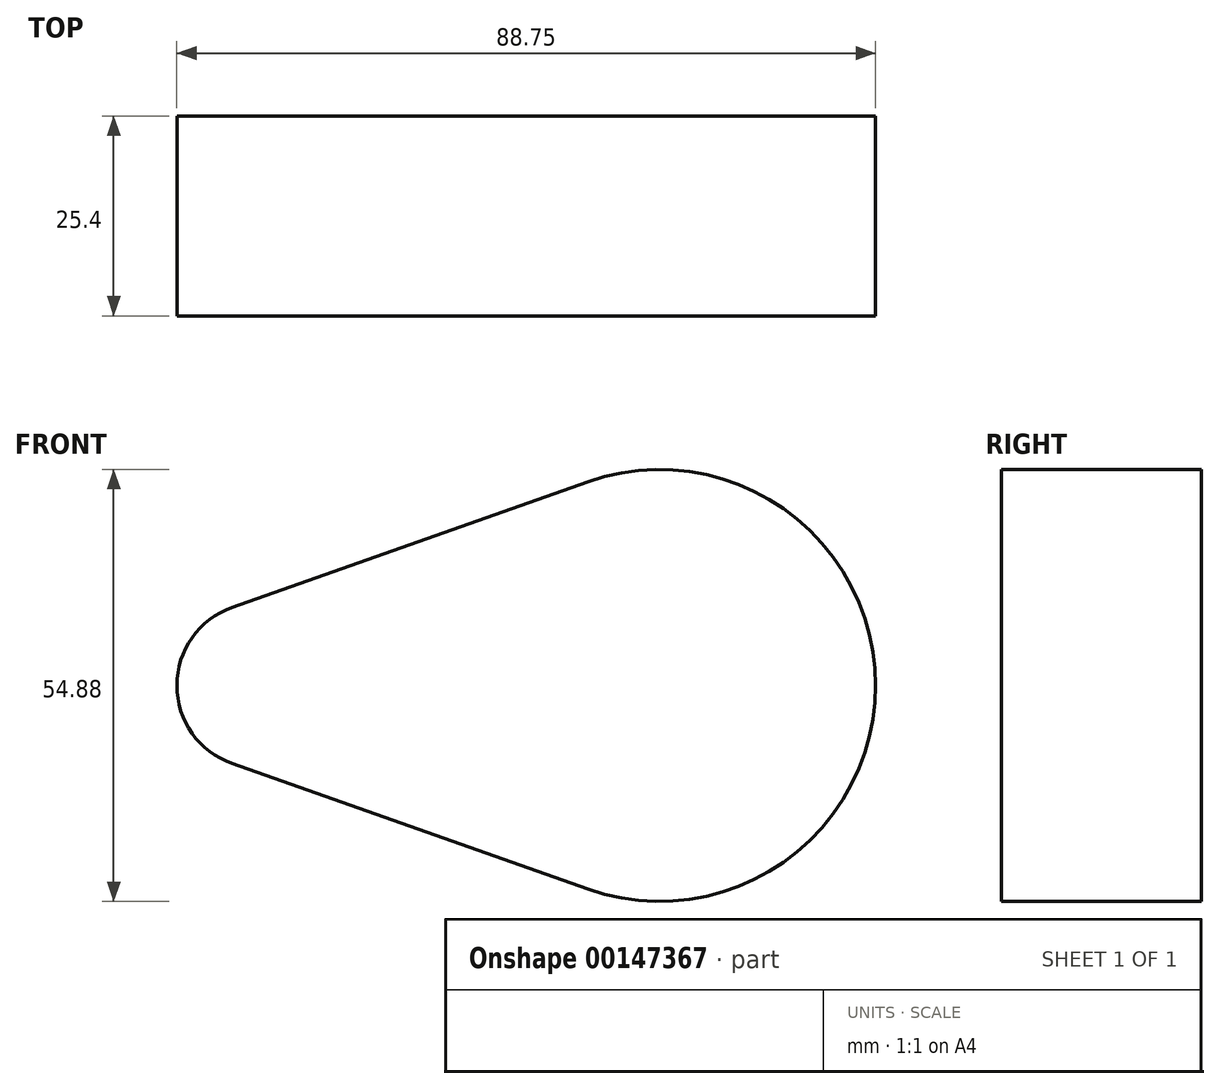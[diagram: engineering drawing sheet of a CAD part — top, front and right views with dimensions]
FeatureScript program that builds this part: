
annotation { "Feature Type Name" : "Feature", "Feature Type Description" : "" }
export const myFeature = defineFeature(function(context is Context, id is Id, definition is map)
    precondition{}
    {
        {
            var Q0;
            Q0=qCreatedBy(makeId("Front.planeOp"),FACE);
            var sketch = newSketch(context, id + "F0", { "sketchPlane" : qUnion([Q0])});
            skCircle(sketch, "E0", {"center": v(0, 0) * mm, "radius": 10.5 * mm});
            skCircle(sketch, "E1", {"center": v(50.8, 0) * mm, "radius": 27.44 * mm});
            skLineSegment(sketch, "E2", {"start": v(57.65, 31.52) * mm, "end": v(-31.52, 0) * mm});
            skLineSegment(sketch, "E3", {"start": v(66.76, -34.74) * mm, "end": v(-31.5, -0.01) * mm});
            skLineSegment(sketch, "E4.0", {"start": v(55.53, 37.5) * mm, "end": v(-33.64, 5.99) * mm});
            skLineSegment(sketch, "E5.0", {"start": v(64.65, -40.73) * mm, "end": v(-33.6, -6) * mm});
            skSolve(sketch);
        }
        {
            var Q0;
            Q0 = qSketchRegion(id + "F0", true);
            extrude(context, id + "F1", {"entities" : qUnion([Q0]), "depth" : 25.4 * mm});
        }
    });
